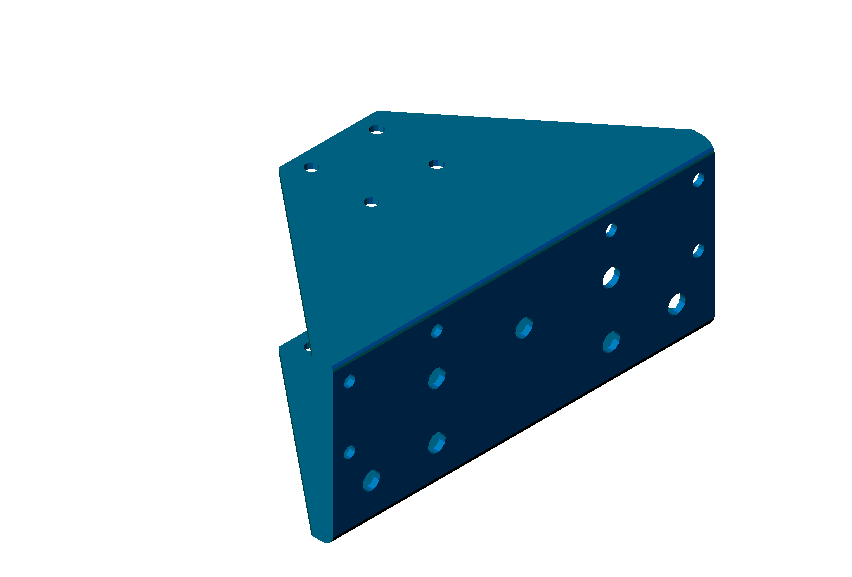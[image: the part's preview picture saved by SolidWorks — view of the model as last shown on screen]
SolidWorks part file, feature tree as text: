
SOLIDWORKS PART (.sldprt)
format: sldprt  version: not decoded by parser v0  size: 403,968 bytes
history: native  units: mm
features: sketch x5, sheet_metal_op x3, cut_extrude x2, material x1, plane x1 + 2 further entries (+12 scaffold rows collapsed)
feature tree (26):
  scaffold x12  (default folders/planes/origin — collapsed)
  material  "Material <not specified>"
  plane  "Side"
  sketch  "Sketch5"  dims[c1.D1=~247.818534mm c2.D1=114.3mm c2.D2=444.5mm c2.D3=114.3mm c2.D4=~137.760912mm c2.D5=~166.874553mm c2.D6=~264.692356mm c2.D7=~280.877123mm c3.D4=215.392mm c3.D5=621.792mm]
  sketch  "Sketch4"  dims[c1.D1=~13.49375mm c1.D2=~13.49375mm c1.D3=~16.66875mm c1.D4=~16.66875mm c1.D5=~13.49375mm c1.D6=~16.66875mm c1.D7=~13.49375mm c1.D8=~13.49375mm c2.D2=20.6375mm c2.D3=20.6375mm c2.D4=~13.49375mm c3.D3=20.6375mm c3.D5=~13.49375mm c3.D6=20.6375mm c3.D7=~13.49375mm c3.D8=20.6375mm c3.D9=~13.49375mm c3.D10=~13.49375mm c4.D6=20.6375mm c4.D7=20.6375mm c4.D8=20.6375mm c4.D3=60.325mm c4.D4=60.325mm c4.D5=101.6mm c5.D6=203.2mm c5.D7=406.4mm c5.D8=31.75mm c5.D3=101.6mm c5.D4=203.2mm c5.D5=120.65mm c6.D3=355.6mm c6.D5=406.4mm c6.D6=39.6875mm c6.D7=80.9625mm c6.D8=104.775mm c6.D9=131.7625mm c6.D10=152.4mm c7.D6=41.275mm c7.D7=65.0875mm c7.D8=112.7125mm c7.D9=47.625mm]
  sheet_metal_op  "Sheet-Metal1"  Thickness=6.35mm
  sheet_metal_op  "Base-Flange1"
  sketch  "Sketch7"  dims[c1.D1=187.325mm c2.D1=6.35mm c2.D4=90.0deg c2.D5=1.0 c2.D8=3.175mm c2.D9=3.175mm]
  sheet_metal_op  "SketchBend2"
  cut_extrude  "Web Holes"  [1 undecoded]
  sketch  "Sketch8"  dims[c1.D2=~28.02646mm c1.D3=~28.02646mm c1.D4=~13.49375mm c1.D1=139.7mm c2.D2=69.85mm c2.D3=76.2mm]
  cut_extrude  "Flg Holes"  [1 undecoded]
  "Flat-Pattern1"
  sketch  "Bend-Lines1"
  "Flatten-<SketchBend2>1"
decode coverage: 5 of 10 modeling features carry decoded parameters; 2 rows unclassified (native names shown)
note: ~ marks probable driven/reference dimensions
note: 2 parameter values undecoded
note: suppression state not decoded; provenance and decode notes live in map.json
